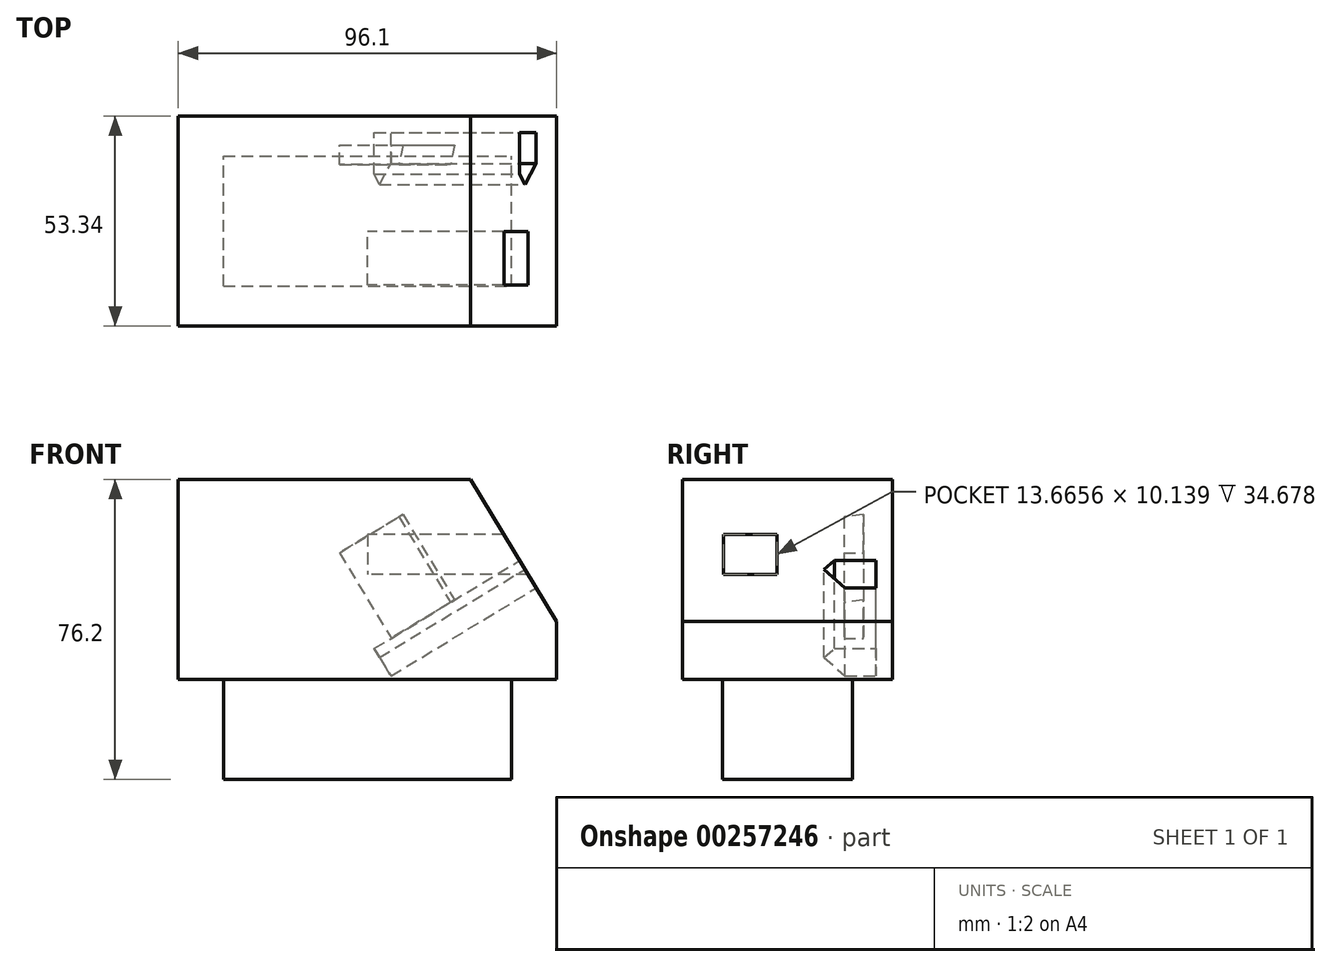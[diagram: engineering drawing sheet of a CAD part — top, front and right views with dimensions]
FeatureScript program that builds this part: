
annotation { "Feature Type Name" : "Feature", "Feature Type Description" : "" }
export const myFeature = defineFeature(function(context is Context, id is Id, definition is map)
    precondition{}
    {
        {
            var Q0;
            Q0=qCreatedBy(makeId("Top.planeOp"),FACE);
            var sketch = newSketch(context, id + "F0", { "sketchPlane" : qUnion([Q0])});
            skLineSegment(sketch, "E0.bottom", {"start": v(-48.05, 26.67) * mm, "end": v(48.05, 26.67) * mm});
            skLineSegment(sketch, "E0.top", {"start": v(-48.05, -26.67) * mm, "end": v(48.05, -26.67) * mm});
            skLineSegment(sketch, "E0.left", {"start": v(-48.05, 26.67) * mm, "end": v(-48.05, -26.67) * mm});
            skLineSegment(sketch, "E0.right", {"start": v(48.05, 26.67) * mm, "end": v(48.05, -26.67) * mm});
            skPoint(sketch, "E0.middle", {"position": v(0, 0) * mm});
            skSolve(sketch);
        }
        {
            var Q0;
            Q0 = qSketchRegion(id + "F0", true);
            extrude(context, id + "F1", {"entities" : qUnion([Q0]), "depth" : 50.8 * mm});
        }
        {
            var Q0;
            Q0=qCreatedBy(makeId("Top.planeOp"),FACE);
            var sketch = newSketch(context, id + "F2", { "sketchPlane" : qUnion([Q0])});
            skLineSegment(sketch, "E1.bottom", {"start": v(-36.59, -16.53) * mm, "end": v(36.59, -16.53) * mm});
            skLineSegment(sketch, "E1.top", {"start": v(-36.59, 16.53) * mm, "end": v(36.59, 16.53) * mm});
            skLineSegment(sketch, "E1.left", {"start": v(-36.59, -16.53) * mm, "end": v(-36.59, 16.53) * mm});
            skLineSegment(sketch, "E1.right", {"start": v(36.59, -16.53) * mm, "end": v(36.59, 16.53) * mm});
            skPoint(sketch, "E1.middle", {"position": v(0, 0) * mm});
            skSolve(sketch);
        }
        {
            var Q0;
            Q0 = qSketchRegion(id + "F2", true);
            extrude(context, id + "F3", {"entities" : qUnion([Q0]), "operationType" : NewBodyOperationType.ADD, "oppositeDirection" : true, "depth" : 25.4 * mm});
        }
        {
            var Q0;
            Q0=qCreatedBy(makeId("Right.planeOp"),FACE);
            var sketch = newSketch(context, id + "F4", { "sketchPlane" : qUnion([Q0])});
            skLineSegment(sketch, "E2.bottom", {"start": v(-16.31, 36.8) * mm, "end": v(-2.64, 36.8) * mm});
            skLineSegment(sketch, "E2.top", {"start": v(-16.31, 26.67) * mm, "end": v(-2.64, 26.67) * mm});
            skLineSegment(sketch, "E2.left", {"start": v(-16.31, 36.8) * mm, "end": v(-16.31, 26.67) * mm});
            skLineSegment(sketch, "E2.right", {"start": v(-2.64, 36.8) * mm, "end": v(-2.64, 26.67) * mm});
            skSolve(sketch);
        }
        {
            var Q0;
            Q0 = qSketchRegion(id + "F4", true);
            extrude(context, id + "F5", {"entities" : qUnion([Q0]), "operationType" : NewBodyOperationType.REMOVE, "endBound" : BoundingType.THROUGH_ALL, "depth" : 38.1 * mm});
        }
        {
            var Q0;
            Q0=makeQuery(id+"F1.opExtrude","SWEPT_FACE",FACE,{"disambiguationData":[OSD([sQuery(id+"F0.wireOp",EDGE,"E0.bottom")])]});
            var sketch = newSketch(context, id + "F6", { "sketchPlane" : qUnion([Q0])});
            skLineSegment(sketch, "E3", {"start": v(-48.05, 14.73) * mm, "end": v(-26.2, 50.8) * mm});
            skLineSegment(sketch, "E4", {"start": v(-48.05, 14.73) * mm, "end": v(-48.05, 50.8) * mm});
            skLineSegment(sketch, "E5", {"start": v(-48.05, 50.8) * mm, "end": v(-26.2, 50.8) * mm});
            skSolve(sketch);
        }
        {
            var Q0;
            Q0 = qSketchRegion(id + "F6", true);
            extrude(context, id + "F7", {"entities" : qUnion([Q0]), "operationType" : NewBodyOperationType.REMOVE, "endBound" : BoundingType.THROUGH_ALL, "oppositeDirection" : true, "depth" : 25.4 * mm});
        }
        {
            var Q0;
            Q0=makeQuery(id+"F7.boolean.opBoolean","COPY",FACE,{"derivedFrom":makeQuery(id+"F7.opExtrude","SWEPT_FACE",FACE,{"disambiguationData":[OSD([sQuery(id+"F6.wireOp",EDGE,"E3")])]})});
            var sketch = newSketch(context, id + "F8", { "sketchPlane" : qUnion([Q0])});
            skLineSegment(sketch, "E6", {"start": v(9.26, 3.21) * mm, "end": v(11.9, 5.79) * mm});
            skLineSegment(sketch, "E7", {"start": v(9.26, 3.21) * mm, "end": v(14.67, -2.34) * mm});
            skLineSegment(sketch, "E8", {"start": v(11.9, 5.79) * mm, "end": v(22.48, 5.79) * mm});
            skLineSegment(sketch, "E9", {"start": v(14.67, -2.34) * mm, "end": v(22.48, -2.34) * mm});
            skLineSegment(sketch, "E10", {"start": v(22.48, 5.79) * mm, "end": v(22.48, -2.34) * mm});
            skSolve(sketch);
        }
        {
            var Q0;
            Q0=makeQuery(id+"F8.imprint","IMPRINT",FACE,{"disambiguationData":[TD([[makeQuery(id+"F8.imprint","IMPRINT",EDGE,{"derivedFrom":sQuery(id+"F8.wireOp",EDGE,"E6")}),-1.0]])]});
            extrude(context, id + "F9", {"entities" : qUnion([Q0]), "operationType" : NewBodyOperationType.REMOVE, "oppositeDirection" : true, "depth" : 43.18 * mm});
        }
        {
            var Q0;
            Q0=makeQuery(id+"F9.boolean.opBoolean","COPY",FACE,{"derivedFrom":makeQuery(id+"F9.opExtrude","SWEPT_FACE",FACE,{"disambiguationData":[OSD([sQuery(id+"F8.wireOp",EDGE,"E8")])]})});
            var sketch = newSketch(context, id + "F10", { "sketchPlane" : qUnion([Q0])});
            skLineSegment(sketch, "E11", {"start": v(28.23, -14.34) * mm, "end": v(10.62, -14.34) * mm});
            skLineSegment(sketch, "E12", {"start": v(10.62, -14.34) * mm, "end": v(10.62, -19.3) * mm});
            skLineSegment(sketch, "E13", {"start": v(10.62, -19.3) * mm, "end": v(29.44, -19.3) * mm});
            skLineSegment(sketch, "E14", {"start": v(29.44, -19.3) * mm, "end": v(28.23, -14.34) * mm});
            skSolve(sketch);
        }
        {
            var Q0;
            Q0 = qSketchRegion(id + "F10", true);
            extrude(context, id + "F11", {"entities" : qUnion([Q0]), "operationType" : NewBodyOperationType.REMOVE, "oppositeDirection" : true, "depth" : 25.4 * mm, "offsetDistance" : 25.4 * mm});
        }
    });
